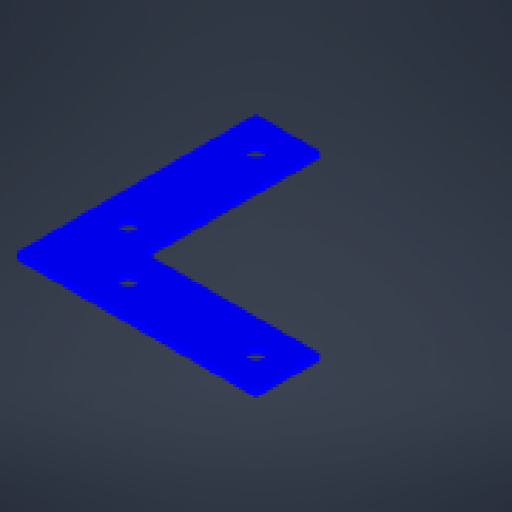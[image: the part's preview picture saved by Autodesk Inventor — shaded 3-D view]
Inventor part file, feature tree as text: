
AUTODESK INVENTOR PART (.ipt)
format: ipt  version: 2024 (Build 280153000, 153)  size: 154,112 bytes
history: native  units: mm
features: other x1, extrude x1, sketch x1
ambient origin geometry x8: Origin, YZ Plane, XZ Plane, XY Plane, X Axis, Y Axis, Z Axis, Center Point
bodies: Body1 (feature_tree)
feature tree (3):
  other  "Твердое тело1"
  extrude  "Выдавливание1"  Depth=5.0mm
  sketch  "Эскиз1"
